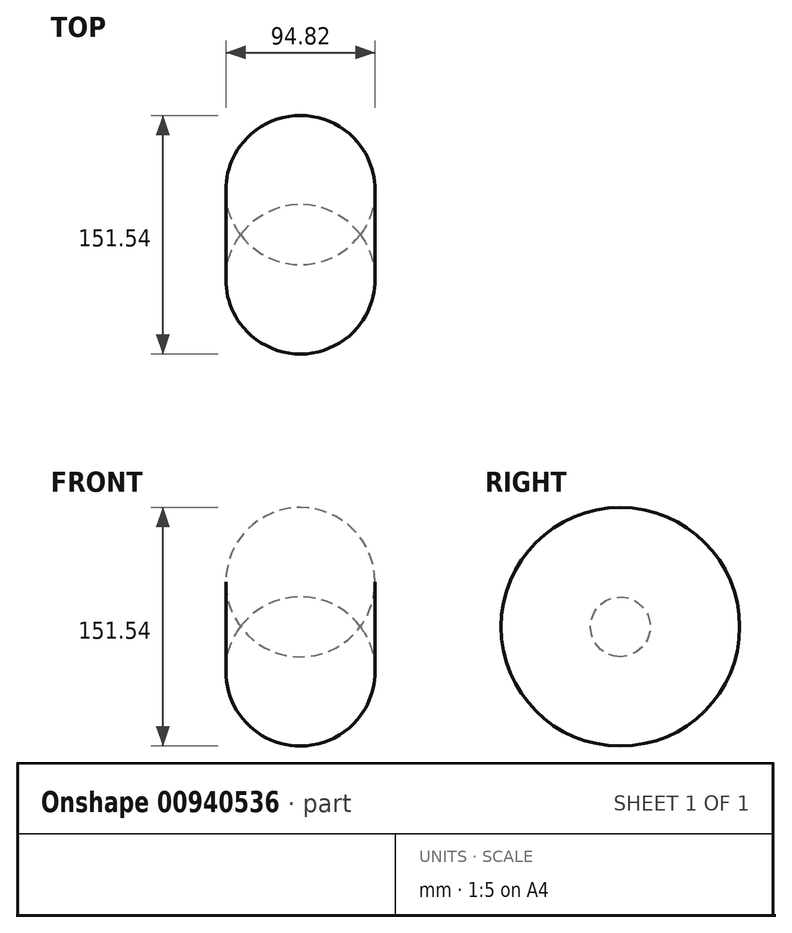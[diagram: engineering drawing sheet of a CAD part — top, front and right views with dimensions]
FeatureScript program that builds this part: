
annotation { "Feature Type Name" : "Feature", "Feature Type Description" : "" }
export const myFeature = defineFeature(function(context is Context, id is Id, definition is map)
    precondition{}
    {
        {
            var Q0;
            Q0=qCreatedBy(makeId("Front.planeOp"),FACE);
            var sketch = newSketch(context, id + "F0", { "sketchPlane" : qUnion([Q0])});
            skArc(sketch, "E0", {"start": v(-38, 0) * mm, "mid": v(0, -19.05) * mm, "end": v(38, 0) * mm});
            skLineSegment(sketch, "E1", {"start": v(-38, 0) * mm, "end": v(38, 0) * mm});
            skSolve(sketch);
        }
        {
            var Q0;
            Q0 = qSketchRegion(id + "F0", true);
            var Q1;
            Q1=sQuery(id+"F0.wireOp",EDGE,"E1");
            revolve(context, id + "F1", {"surfaceOperationType" : NewSurfaceOperationType.NEW, "entities" : qUnion([Q0]), "axis" : qUnion([Q1]), "revolveType" : RevolveType.FULL});
        }
    });
